# Revit family: OpenUnit-Vitra-ValarteSeries-62252+62253+62254
name_source: partatom
category: Furniture Systems
revit_build: Autodesk Revit 2017 (Build: 20160225_1515(x64)
units: mm (PartAtom-declared; Revit-internal decimal feet)

## family parameters
Cut with Voids When Loaded = No
Host = Face
OmniClass Number = 23.40.20.27.11
OmniClass Title = Shelves
Part Type = Normal
Room Calculation Point = No
Round Connector Dimension = Use Diameter
Shared = Yes

## types (3) — shared parameters
BIMobject category = Furniture - Shelving & Storage
Construction Type = Face Mounted
Default Elevation = 850 mm  [stored 2.78871 ft]
Depth(mm) = 200 mm  [stored 0.656168 ft]
Description = Valarte Open Unit
Design country = Turkey
Height(mm) = 1135 mm  [stored 3.72375 ft]
IFC Classification = Furnishing Element
Manufacturer = Vitra
Manufacturer name = Vitra
NBS Referans Code = 35-77-06
NBS Referans Description = Bathroom Shelves
Nominal height = 0.000
Nominal width = 0.000
OmniClass Code = 23-21 19 00
OmniClass Description = Casework
Product certification = https://vitraglobal.com
Product data url = https://www.vitra.co.uk
Product family = Valarte
Product group = Bathroom Furniture
Technical description = https://www.vitra.co.uk
UNSPSC Code = 56
UNSPSC Description = Furniture and Furnishings
URL = https://vitraglobal.com
Uniclass 1.4 Code = L72141
Uniclass 1.4 Description = Cabinets
Uniclass 2.0 Code = PR-35-77-06
Uniclass 2.0 Description = Bathroom Shelves
Uniformat II Description = Fixed Furnishings
Warranty Period (Year) = 2
Weight Net (kg) = 23,000
Width(mm) = 535 mm  [stored 1.75525 ft]
Youtube = https://www.youtube.com

## per-type parameters (varying)
| type | Article No. (default) | Model | Primary Material | Product SKU |
| OpenUnit-Vitra-ValarteSeries_62252 | 62252 | 62252 | Vitra-MattWhite | 62252 |
| OpenUnit-Vitra-ValarteSeries_62253 | 62253 | 62253 | Vitra-MattGrey | 62253 |
| OpenUnit-Vitra-ValarteSeries_62254 | 62254 | 62254 | Vitra-MattIvory | 62254 |

note: [stored X ft] marks values corroborated as IEEE doubles in the binary element streams (Revit-internal decimal feet)

## geometry (parser evidence)
native form markers: Sweep x3
no freeform markers — native parametric forms only
